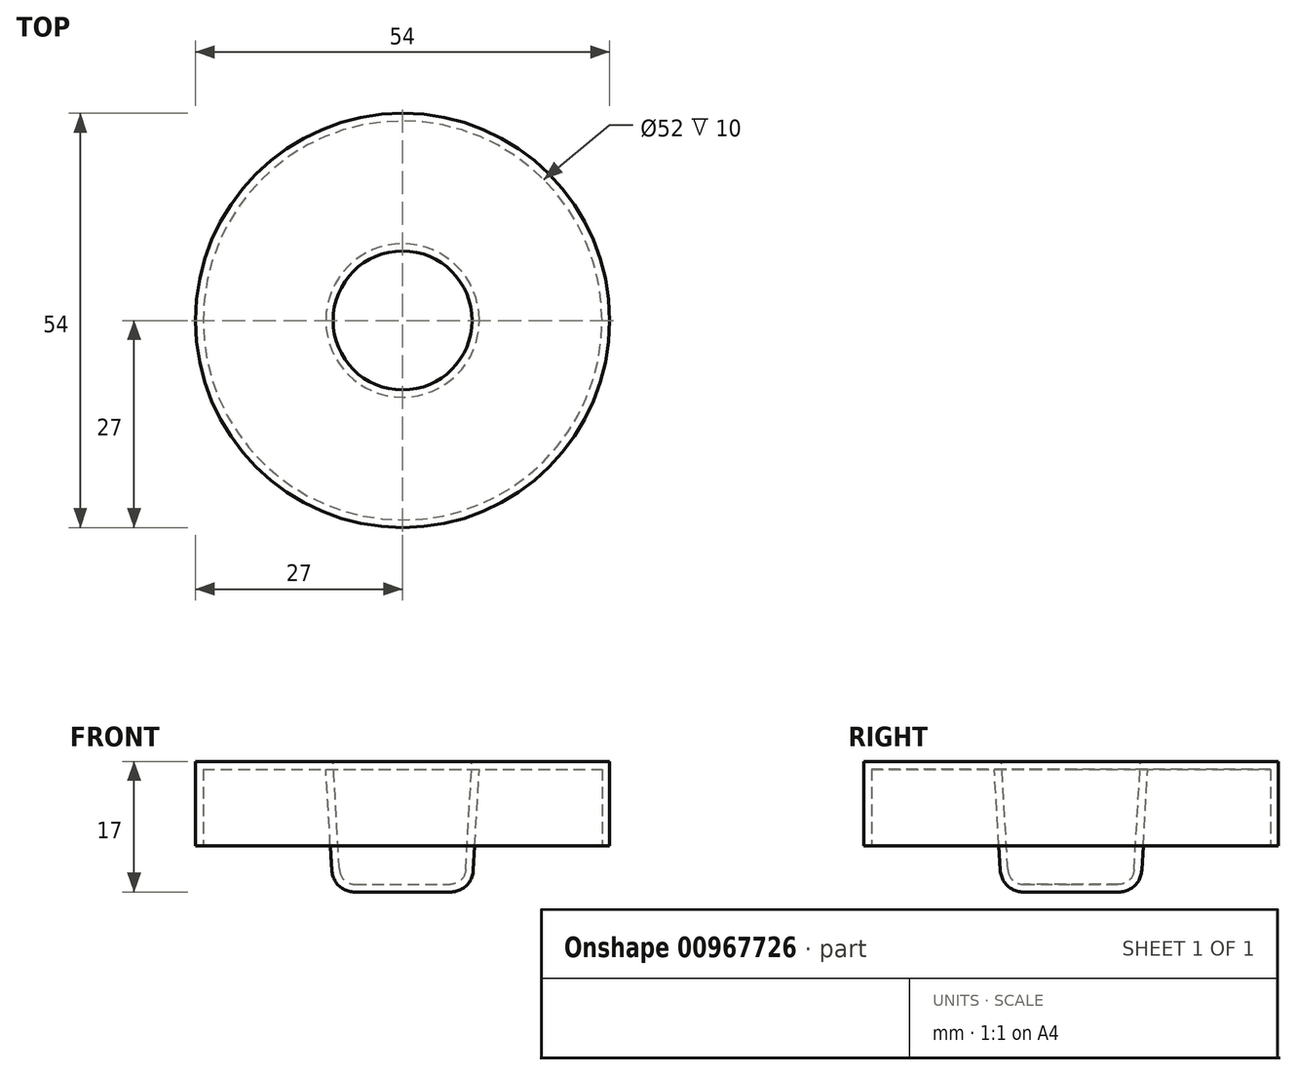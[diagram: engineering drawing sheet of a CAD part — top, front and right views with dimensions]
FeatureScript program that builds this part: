
annotation { "Feature Type Name" : "Feature", "Feature Type Description" : "" }
export const myFeature = defineFeature(function(context is Context, id is Id, definition is map)
    precondition{}
    {
        {
            var Q0;
            Q0=qCreatedBy(makeId("Front.planeOp"),FACE);
            var sketch = newSketch(context, id + "F0", { "sketchPlane" : qUnion([Q0])});
            skLineSegment(sketch, "E0", {"start": v(0, 0) * mm, "end": v(6.23, 0) * mm});
            skLineSegment(sketch, "E1", {"start": v(8.23, 1.88) * mm, "end": v(9.06, 16) * mm});
            skLineSegment(sketch, "E2", {"start": v(9.06, 16) * mm, "end": v(27, 16) * mm});
            skLineSegment(sketch, "E3", {"start": v(27, 16) * mm, "end": v(27, 5) * mm});
            skLineSegment(sketch, "E4", {"start": v(27, 5) * mm, "end": v(26, 5) * mm});
            skLineSegment(sketch, "E5", {"start": v(26, 5) * mm, "end": v(26, 15) * mm});
            skLineSegment(sketch, "E6", {"start": v(26, 15) * mm, "end": v(10, 15) * mm});
            skLineSegment(sketch, "E7", {"start": v(10, 15) * mm, "end": v(9.22, 1.82) * mm});
            skLineSegment(sketch, "E8", {"start": v(6.23, -1) * mm, "end": v(0, -1) * mm});
            skLineSegment(sketch, "E9", {"start": v(0, -1) * mm, "end": v(0, 0) * mm});
            skPoint(sketch, "E10.visualSharp", {"position": v(8.11, 0) * mm});
            skArc(sketch, "E10.filletArc", {"start": v(6.23, 0) * mm, "mid": v(7.6, 0.54) * mm, "end": v(8.23, 1.88) * mm});
            skPoint(sketch, "E11.visualSharp", {"position": v(9.06, -1) * mm});
            skArc(sketch, "E11.filletArc", {"start": v(6.23, -1) * mm, "mid": v(8.29, -0.18) * mm, "end": v(9.22, 1.82) * mm});
            skSolve(sketch);
        }
        {
            var Q0;
            Q0=makeQuery(id+"F0.imprint","IMPRINT",FACE,{"disambiguationData":[TD([[makeQuery(id+"F0.imprint","IMPRINT",EDGE,{"derivedFrom":sQuery(id+"F0.wireOp",EDGE,"E0")}),-1.0]])]});
            var Q1;
            Q1=sQuery(id+"F0.wireOp",EDGE,"E7");
            var Q2;
            Q2=sQuery(id+"F0.wireOp",EDGE,"E3");
            var Q3;
            Q3=sQuery(id+"F0.wireOp",EDGE,"E2");
            var Q4;
            Q4=sQuery(id+"F0.wireOp",EDGE,"E8");
            var Q5;
            Q5=sQuery(id+"F0.wireOp",EDGE,"E4");
            var Q6;
            Q6=sQuery(id+"F0.wireOp",EDGE,"E10.filletArc");
            var Q7;
            Q7=sQuery(id+"F0.wireOp",EDGE,"E1");
            var Q8;
            Q8=sQuery(id+"F0.wireOp",EDGE,"E11.filletArc");
            var Q9;
            Q9=sQuery(id+"F0.wireOp",EDGE,"E6");
            var Q10;
            Q10=sQuery(id+"F0.wireOp",EDGE,"E0");
            var Q11;
            Q11=sQuery(id+"F0.wireOp",EDGE,"E5");
            var Q12;
            Q12=sQuery(id+"F0.wireOp",EDGE,"E9");
            revolve(context, id + "F1", {"surfaceOperationType" : NewSurfaceOperationType.NEW, "entities" : qUnion([Q0]), "surfaceEntities" : qUnion([Q1, Q2, Q3, Q4, Q5, Q6, Q7, Q8, Q9, Q10, Q11]), "axis" : qUnion([Q12]), "revolveType" : RevolveType.FULL});
        }
    });
